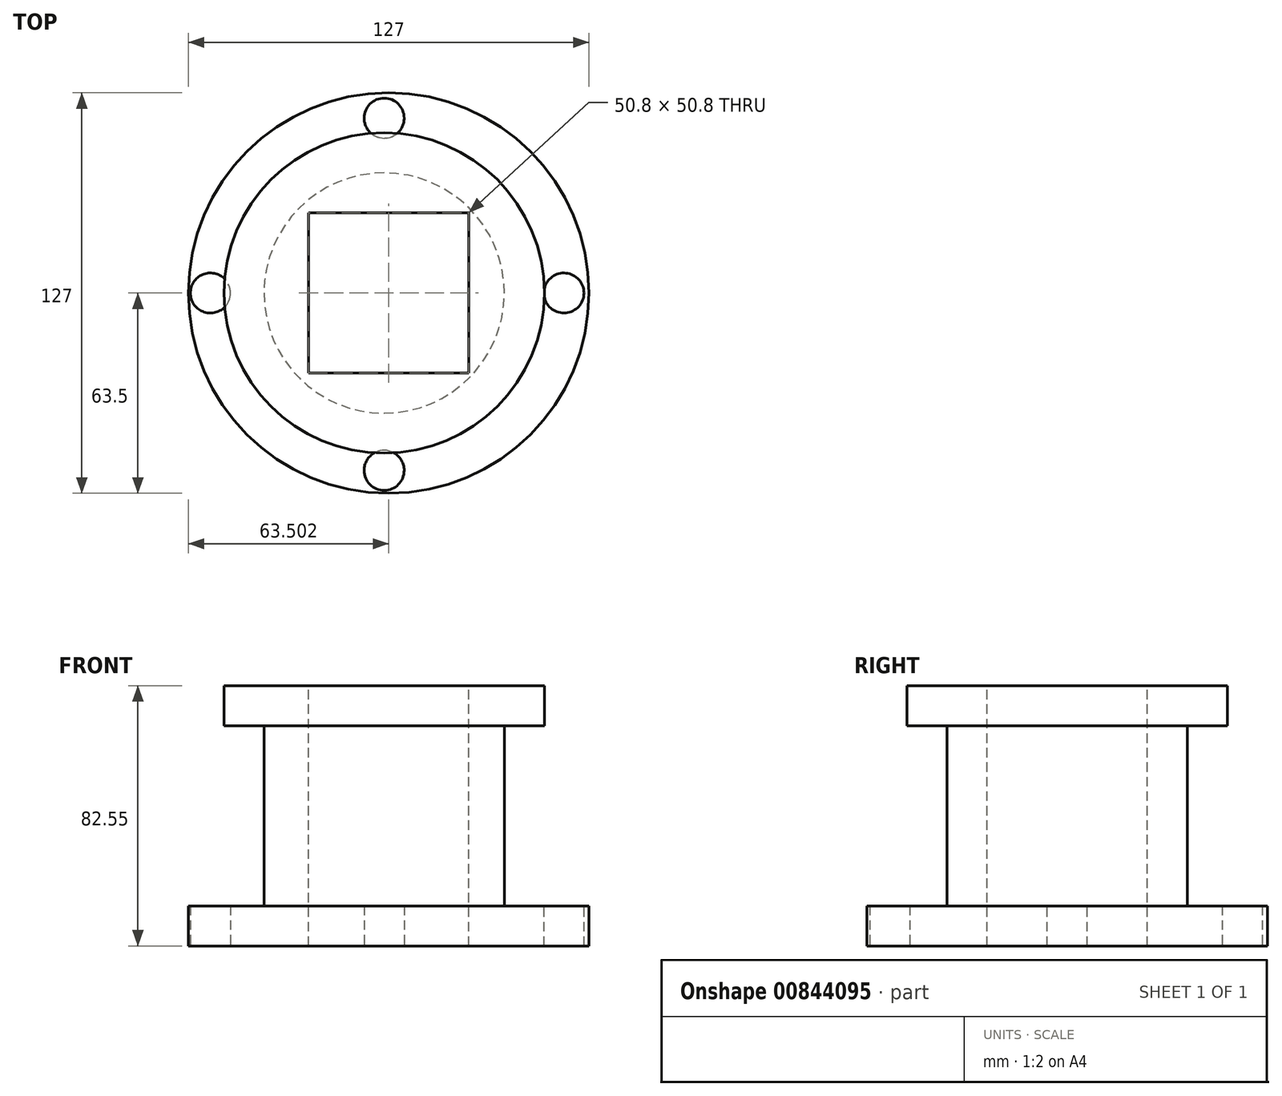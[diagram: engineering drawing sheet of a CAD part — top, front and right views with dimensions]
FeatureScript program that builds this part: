
annotation { "Feature Type Name" : "Feature", "Feature Type Description" : "" }
export const myFeature = defineFeature(function(context is Context, id is Id, definition is map)
    precondition{}
    {
        {
            var Q0;
            Q0=qCreatedBy(makeId("Top.planeOp"),FACE);
            var sketch = newSketch(context, id + "F0", { "sketchPlane" : qUnion([Q0])});
            skCircle(sketch, "E0", {"center": v(1.43, 0) * mm, "radius": 63.5 * mm});
            skSolve(sketch);
        }
        {
            var Q0;
            Q0 = qSketchRegion(id + "F0", true);
            extrude(context, id + "F1", {"entities" : qUnion([Q0]), "depth" : 12.7 * mm, "offsetDistance" : 25.4 * mm});
        }
        {
            var Q0;
            Q0=makeQuery(id+"F1.opExtrude","CAP_FACE",FACE,{"disambiguationData":[OSD([sQuery(id+"F0.wireOp",EDGE,"E0")])],"isStart":false});
            var sketch = newSketch(context, id + "F2", { "sketchPlane" : qUnion([Q0])});
            skCircle(sketch, "E1", {"center": v(0, 0) * mm, "radius": 38.1 * mm});
            skSolve(sketch);
        }
        {
            var Q0;
            Q0 = qSketchRegion(id + "F2", true);
            extrude(context, id + "F3", {"entities" : qUnion([Q0]), "operationType" : NewBodyOperationType.ADD, "depth" : 57.15 * mm, "offsetDistance" : 25.4 * mm});
        }
        {
            var Q0;
            Q0=makeQuery(id+"F3.opExtrude","CAP_FACE",FACE,{"disambiguationData":[OSD([sQuery(id+"F2.wireOp",EDGE,"E1")])],"isStart":false});
            var sketch = newSketch(context, id + "F4", { "sketchPlane" : qUnion([Q0])});
            skCircle(sketch, "E2", {"center": v(0, 0) * mm, "radius": 50.8 * mm});
            skSolve(sketch);
        }
        {
            var Q0;
            Q0 = qSketchRegion(id + "F4", true);
            extrude(context, id + "F5", {"entities" : qUnion([Q0]), "operationType" : NewBodyOperationType.ADD, "depth" : 12.7 * mm, "offsetDistance" : 25.4 * mm});
        }
        {
            var Q0;
            Q0=makeQuery(id+"F1.opExtrude","CAP_FACE",FACE,{"disambiguationData":[OSD([sQuery(id+"F0.wireOp",EDGE,"E0")])],"isStart":true});
            var sketch = newSketch(context, id + "F6", { "sketchPlane" : qUnion([Q0])});
            skCircle(sketch, "E3", {"center": v(0, -55.47) * mm, "radius": 6.35 * mm});
            skSolve(sketch);
        }
        {
            var Q0;
            Q0 = qSketchRegion(id + "F6", true);
            extrude(context, id + "F7", {"entities" : qUnion([Q0]), "operationType" : NewBodyOperationType.REMOVE, "oppositeDirection" : true, "depth" : 25.4 * mm, "offsetDistance" : 25.4 * mm});
        }
        {
            var Q0;
            Q0=makeQuery(id+"F1.opExtrude","CAP_FACE",FACE,{"disambiguationData":[OSD([sQuery(id+"F0.wireOp",EDGE,"E0")])],"isStart":false});
            var sketch = newSketch(context, id + "F8", { "sketchPlane" : qUnion([Q0])});
            skCircle(sketch, "E4", {"center": v(57, 0) * mm, "radius": 6.35 * mm});
            skSolve(sketch);
        }
        {
            var Q0;
            Q0 = qSketchRegion(id + "F8", true);
            extrude(context, id + "F9", {"entities" : qUnion([Q0]), "operationType" : NewBodyOperationType.REMOVE, "oppositeDirection" : true, "depth" : 25.4 * mm, "offsetDistance" : 25.4 * mm});
        }
        {
            var Q0;
            Q0=makeQuery(id+"F1.opExtrude","CAP_FACE",FACE,{"disambiguationData":[OSD([sQuery(id+"F0.wireOp",EDGE,"E0")])],"isStart":true});
            var sketch = newSketch(context, id + "F10", { "sketchPlane" : qUnion([Q0])});
            skCircle(sketch, "E5", {"center": v(0, 56.24) * mm, "radius": 6.35 * mm});
            skPoint(sketch, "E6.center.orphan", {"position": v(-55.72, 0) * mm});
            skSolve(sketch);
        }
        {
            var Q0;
            Q0=makeQuery(id+"F10.imprint","IMPRINT",FACE,{"disambiguationData":[TD([[makeQuery(id+"F10.imprint","IMPRINT",EDGE,{"derivedFrom":sQuery(id+"F10.wireOp",EDGE,"E5")}),1.0]])]});
            extrude(context, id + "F11", {"entities" : qUnion([Q0]), "operationType" : NewBodyOperationType.REMOVE, "oppositeDirection" : true, "depth" : 25.4 * mm, "offsetDistance" : 25.4 * mm});
        }
        {
            var Q0;
            Q0=makeQuery(id+"F10.imprint","IMPRINT",FACE,{"disambiguationData":[TD([[makeQuery(id+"F10.imprint","IMPRINT",EDGE,{"derivedFrom":sQuery(id+"F10.wireOp",EDGE,"E5")}),-1.0]])]});
            var sketch = newSketch(context, id + "F12", { "sketchPlane" : qUnion([Q0])});
            skCircle(sketch, "E7", {"center": v(-55.1, 0) * mm, "radius": 6.35 * mm});
            skSolve(sketch);
        }
        {
            var Q0;
            Q0=makeQuery(id+"F12.imprint","IMPRINT",FACE,{"disambiguationData":[TD([[makeQuery(id+"F12.imprint","IMPRINT",EDGE,{"derivedFrom":sQuery(id+"F12.wireOp",EDGE,"E7")}),1.0]])]});
            extrude(context, id + "F13", {"entities" : qUnion([Q0]), "operationType" : NewBodyOperationType.REMOVE, "oppositeDirection" : true, "depth" : 25.4 * mm, "offsetDistance" : 25.4 * mm});
        }
        {
            var Q0;
            Q0=makeQuery(id+"F5.opExtrude","CAP_FACE",FACE,{"disambiguationData":[OSD([sQuery(id+"F4.wireOp",EDGE,"E2")])],"isStart":false});
            var sketch = newSketch(context, id + "F14", { "sketchPlane" : qUnion([Q0])});
            skLineSegment(sketch, "E8.bottom", {"start": v(26.83, -25.4) * mm, "end": v(-23.97, -25.4) * mm});
            skLineSegment(sketch, "E8.top", {"start": v(26.83, 25.4) * mm, "end": v(-23.97, 25.4) * mm});
            skLineSegment(sketch, "E8.left", {"start": v(26.83, -25.4) * mm, "end": v(26.83, 25.4) * mm});
            skLineSegment(sketch, "E8.right", {"start": v(-23.97, -25.4) * mm, "end": v(-23.97, 25.4) * mm});
            skPoint(sketch, "E8.middle", {"position": v(1.43, 0) * mm});
            skSolve(sketch);
        }
        {
            var Q0;
            Q0 = qSketchRegion(id + "F14", true);
            extrude(context, id + "F15", {"entities" : qUnion([Q0]), "operationType" : NewBodyOperationType.REMOVE, "oppositeDirection" : true, "depth" : 101.6 * mm, "offsetDistance" : 25.4 * mm});
        }
    });
